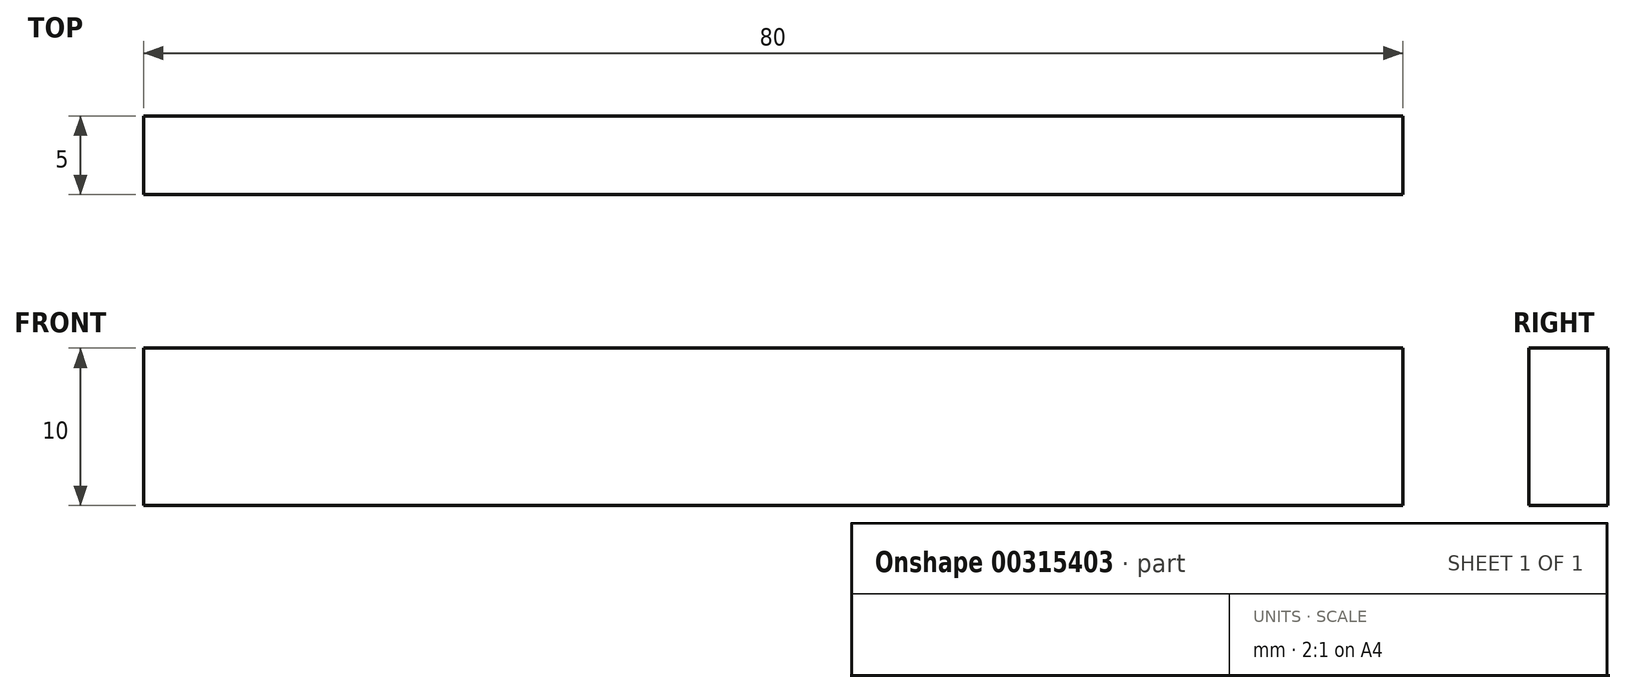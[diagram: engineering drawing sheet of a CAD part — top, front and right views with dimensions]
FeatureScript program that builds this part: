
annotation { "Feature Type Name" : "Feature", "Feature Type Description" : "" }
export const myFeature = defineFeature(function(context is Context, id is Id, definition is map)
    precondition{}
    {
        {
            var Q0;
            Q0=qCreatedBy(makeId("Front.planeOp"),FACE);
            var sketch = newSketch(context, id + "F0", { "sketchPlane" : qUnion([Q0])});
            skLineSegment(sketch, "E0.bottom", {"start": v(-40, 5) * mm, "end": v(40, 5) * mm});
            skLineSegment(sketch, "E0.top", {"start": v(-40, -5) * mm, "end": v(40, -5) * mm});
            skLineSegment(sketch, "E0.left", {"start": v(-40, 5) * mm, "end": v(-40, -5) * mm});
            skLineSegment(sketch, "E0.right", {"start": v(40, 5) * mm, "end": v(40, -5) * mm});
            skPoint(sketch, "E0.middle", {"position": v(0, 0) * mm});
            skSolve(sketch);
        }
        {
            var Q0;
            Q0=makeQuery(id+"F0.imprint","IMPRINT",FACE,{"disambiguationData":[TD([[makeQuery(id+"F0.imprint","IMPRINT",EDGE,{"derivedFrom":sQuery(id+"F0.wireOp",EDGE,"E0.bottom")}),-1.0]])]});
            extrude(context, id + "F1", {"entities" : qUnion([Q0]), "depth" : 5 * mm});
        }
    });
